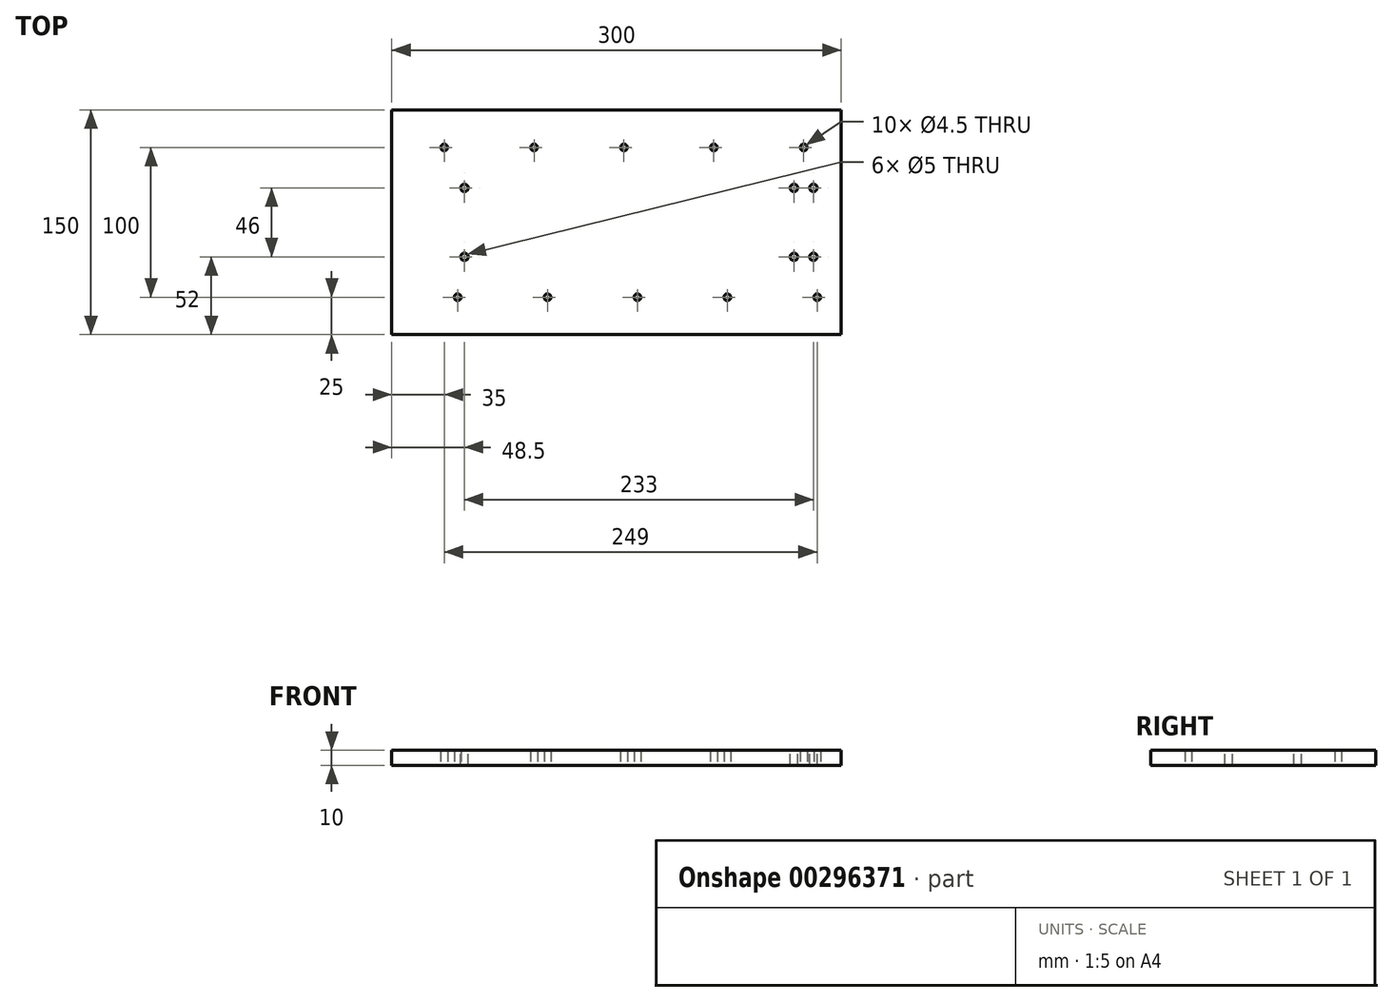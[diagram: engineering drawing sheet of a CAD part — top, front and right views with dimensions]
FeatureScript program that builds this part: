
annotation { "Feature Type Name" : "Feature", "Feature Type Description" : "" }
export const myFeature = defineFeature(function(context is Context, id is Id, definition is map)
    precondition{}
    {
        {
            var Q0;
            Q0=qCreatedBy(makeId("Top.planeOp"),FACE);
            var sketch = newSketch(context, id + "F0", { "sketchPlane" : qUnion([Q0])});
            skLineSegment(sketch, "E0.bottom", {"start": v(150, 75) * mm, "end": v(-150, 75) * mm});
            skLineSegment(sketch, "E0.top", {"start": v(150, -75) * mm, "end": v(-150, -75) * mm});
            skLineSegment(sketch, "E0.left", {"start": v(150, 75) * mm, "end": v(150, -75) * mm});
            skLineSegment(sketch, "E0.right", {"start": v(-150, 75) * mm, "end": v(-150, -75) * mm});
            skPoint(sketch, "E0.middle", {"position": v(0, 0) * mm});
            skLineSegment(sketch, "E1", {"start": v(-150, 0) * mm, "end": v(150, 0) * mm, "construction": true});
            skLineSegment(sketch, "E2", {"start": v(-150, 50) * mm, "end": v(150, 50) * mm, "construction": true});
            skLineSegment(sketch, "E3", {"start": v(-150, -50) * mm, "end": v(150, -50) * mm, "construction": true});
            skPoint(sketch, "E4", {"position": v(125, 50) * mm});
            skPoint(sketch, "E5.1.0.0", {"position": v(65, 50) * mm});
            skPoint(sketch, "E5.2.0.0", {"position": v(5, 50) * mm});
            skPoint(sketch, "E5.3.0.0", {"position": v(-55, 50) * mm});
            skPoint(sketch, "E5.4.0.0", {"position": v(-115, 50) * mm});
            skLineSegment(sketch, "E5.direction1", {"start": v(125, 50) * mm, "end": v(65, 50) * mm, "construction": true});
            skLineSegment(sketch, "E5.direction2", {"start": v(125, 50) * mm, "end": v(125, -50) * mm, "construction": true});
            skPoint(sketch, "E6", {"position": v(134, -50) * mm});
            skPoint(sketch, "E7.1.0.0", {"position": v(74, -50) * mm});
            skPoint(sketch, "E7.2.0.0", {"position": v(14, -50) * mm});
            skPoint(sketch, "E7.3.0.0", {"position": v(-46, -50) * mm});
            skPoint(sketch, "E7.4.0.0", {"position": v(-106, -50) * mm});
            skLineSegment(sketch, "E7.direction1", {"start": v(134, -50) * mm, "end": v(74, -50) * mm, "construction": true});
            skSolve(sketch);
        }
        {
            var Q0;
            Q0 = qSketchRegion(id + "F0", true);
            extrude(context, id + "F1", {"entities" : qUnion([Q0]), "depth" : 10 * mm});
        }
        {
            var Q0;
            Q0=sQuery(id+"F0.wireOp",VERTEX,"E4");
            var Q1;
            Q1=sQuery(id+"F0.wireOp",VERTEX,"E5.1.0.0");
            var Q2;
            Q2=sQuery(id+"F0.wireOp",VERTEX,"E5.3.0.0");
            var Q3;
            Q3=sQuery(id+"F0.wireOp",VERTEX,"E5.4.0.0");
            var Q4;
            Q4=sQuery(id+"F0.wireOp",VERTEX,"E5.4.1.0");
            var Q5;
            Q5=sQuery(id+"F0.wireOp",VERTEX,"E5.3.1.0");
            var Q6;
            Q6=sQuery(id+"F0.wireOp",VERTEX,"E5.2.1.0");
            var Q7;
            Q7=sQuery(id+"F0.wireOp",VERTEX,"E5.1.1.0");
            var Q8;
            Q8=sQuery(id+"F0.wireOp",VERTEX,"E5.0.1.0");
            var Q9;
            Q9=sQuery(id+"F0.wireOp",VERTEX,"E5.2.0.0");
            var Q10;
            Q10=sQuery(id+"F0.wireOp",VERTEX,"E6");
            var Q11;
            Q11=sQuery(id+"F0.wireOp",VERTEX,"E7.direction1.end");
            var Q12;
            Q12=sQuery(id+"F0.wireOp",VERTEX,"E7.2.0.0");
            var Q13;
            Q13=sQuery(id+"F0.wireOp",VERTEX,"E7.3.0.0");
            var Q14;
            Q14=sQuery(id+"F0.wireOp",VERTEX,"E7.4.0.0");
            var Q15;
            Q15=makeQuery(id+"F1.opExtrude","SWEPT_BODY",BODY,{"disambiguationData":[OSD([sQuery(id+"F0.wireOp",EDGE,"E0.bottom"),sQuery(id+"F0.wireOp",EDGE,"E0.top"),sQuery(id+"F0.wireOp",EDGE,"E0.left"),sQuery(id+"F0.wireOp",EDGE,"E0.right")])]});
            hole(context, id + "F2", {"style" : HoleStyle.SIMPLE, "endStyle" : HoleEndStyle.THROUGH, "oppositeDirection" : true, "standardTappedOrClearance" : lookupTablePath({ "standard" : "ISO", "engagement" : "25%", "pitch" : "0.8 mm", "size" : "M5", "type" : "Tapped" }), "standardBlindInLast" : lookupTablePath({ "standard" : "ISO", "engagement" : "25%", "pitch" : "0.8 mm", "size" : "M5", "type" : "Tapped" }), "holeDiameter" : 4.5 * mm, "showTappedDepth" : true, "tappedDepth" : 8 * mm, "tapClearance" : 3, "locations" : qUnion([Q0, Q1, Q2, Q3, Q4, Q5, Q6, Q7, Q8, Q9, Q10, Q11, Q12, Q13, Q14]), "scope" : qUnion([Q15])});
        }
        {
            var Q0;
            Q0=makeQuery(id+"F1.opExtrude","CAP_FACE",FACE,{"disambiguationData":[OSD([sQuery(id+"F0.wireOp",EDGE,"E0.bottom"),sQuery(id+"F0.wireOp",EDGE,"E0.top"),sQuery(id+"F0.wireOp",EDGE,"E0.left"),sQuery(id+"F0.wireOp",EDGE,"E0.right")])],"isStart":false});
            var sketch = newSketch(context, id + "F3", { "sketchPlane" : qUnion([Q0])});
            skLineSegment(sketch, "E8.bottom", {"start": v(118.5, 23) * mm, "end": v(131.5, 23) * mm, "construction": true});
            skLineSegment(sketch, "E8.top", {"start": v(118.5, -23) * mm, "end": v(131.5, -23) * mm, "construction": true});
            skLineSegment(sketch, "E8.left", {"start": v(118.5, 23) * mm, "end": v(118.5, -23) * mm, "construction": true});
            skLineSegment(sketch, "E8.right", {"start": v(131.5, 23) * mm, "end": v(131.5, -23) * mm, "construction": true});
            skPoint(sketch, "E9", {"position": v(118.5, 23) * mm});
            skPoint(sketch, "E10", {"position": v(131.5, 23) * mm});
            skPoint(sketch, "E11", {"position": v(118.5, -23) * mm});
            skPoint(sketch, "E12", {"position": v(131.5, -23) * mm});
            skPoint(sketch, "E13", {"position": v(131.37, 22.95) * mm});
            skLineSegment(sketch, "E14", {"start": v(-101.5, 23) * mm, "end": v(-101.5, -23) * mm, "construction": true});
            skPoint(sketch, "E15", {"position": v(-101.5, 23) * mm});
            skPoint(sketch, "E16", {"position": v(-101.5, -23) * mm});
            skSolve(sketch);
        }
        {
            var Q0;
            Q0=sQuery(id+"F3.wireOp",VERTEX,"E8.left.start");
            var Q1;
            Q1=sQuery(id+"F3.wireOp",VERTEX,"E10");
            var Q2;
            Q2=sQuery(id+"F3.wireOp",VERTEX,"E12");
            var Q3;
            Q3=sQuery(id+"F3.wireOp",VERTEX,"E11");
            var Q4;
            Q4=sQuery(id+"F3.wireOp",VERTEX,"E15");
            var Q5;
            Q5=sQuery(id+"F3.wireOp",VERTEX,"E16");
            var Q6;
            Q6=makeQuery(id+"F1.opExtrude","SWEPT_BODY",BODY,{"disambiguationData":[OSD([sQuery(id+"F0.wireOp",EDGE,"E0.bottom"),sQuery(id+"F0.wireOp",EDGE,"E0.top"),sQuery(id+"F0.wireOp",EDGE,"E0.left"),sQuery(id+"F0.wireOp",EDGE,"E0.right")])]});
            hole(context, id + "F4", {"style" : HoleStyle.SIMPLE, "endStyle" : HoleEndStyle.THROUGH, "standardTappedOrClearance" : lookupTablePath({ "standard" : "ISO", "engagement" : "75%", "pitch" : "1 mm", "size" : "M6", "type" : "Tapped" }), "standardBlindInLast" : lookupTablePath({ "standard" : "ISO", "engagement" : "75%", "pitch" : "1 mm", "size" : "M6", "type" : "Tapped" }), "holeDiameter" : 5 * mm, "showTappedDepth" : true, "tappedDepth" : 9.6 * mm, "tapClearance" : 3, "locations" : qUnion([Q0, Q1, Q2, Q3, Q4, Q5]), "scope" : qUnion([Q6]), "majorDiameter" : 6 * mm});
        }
    });
